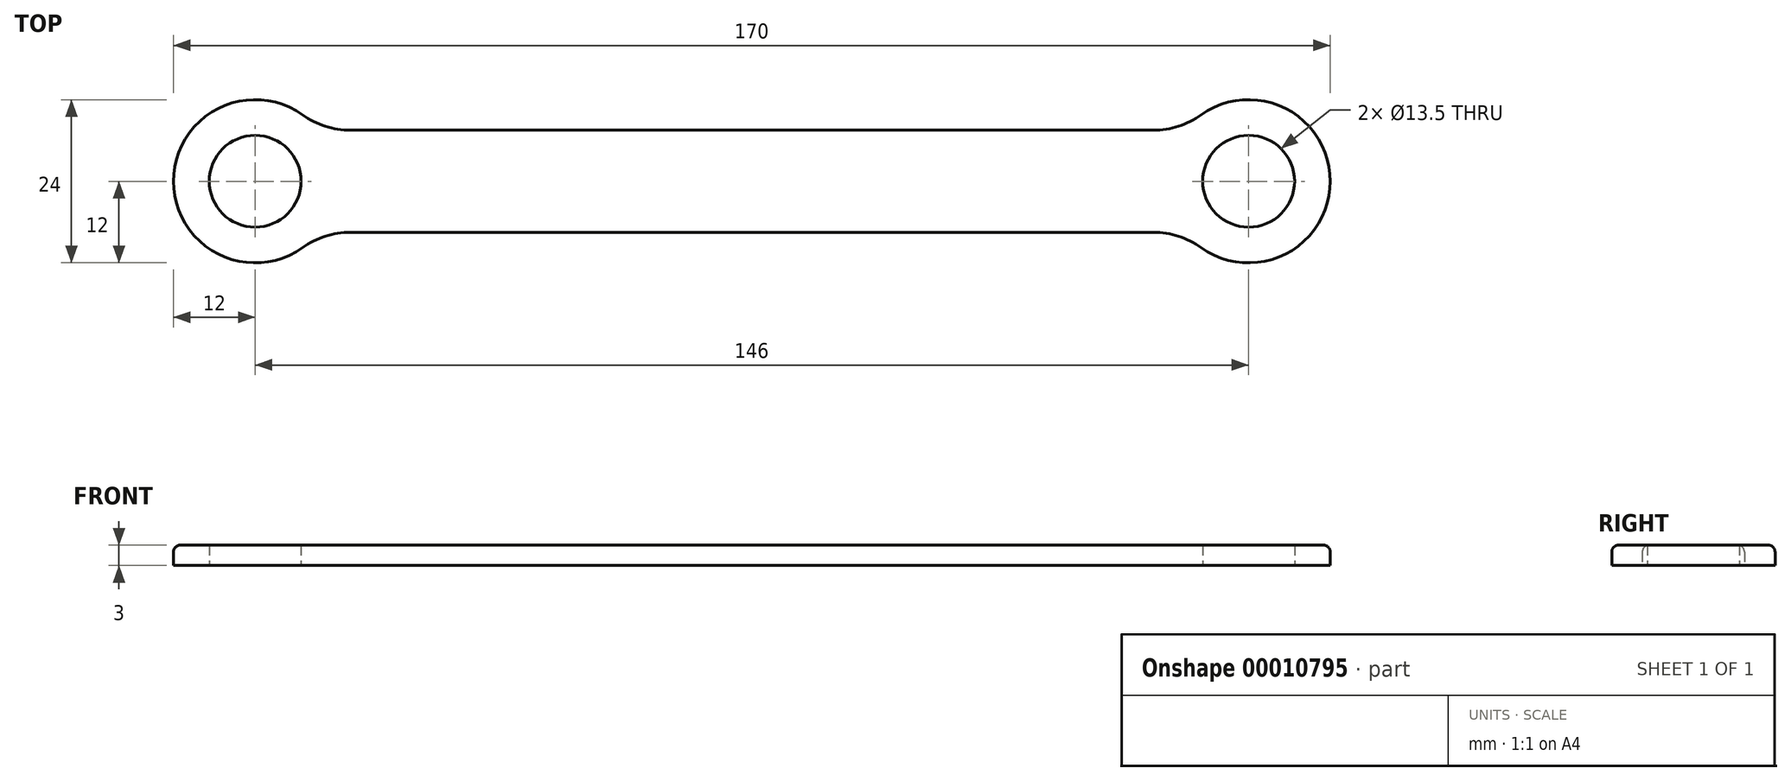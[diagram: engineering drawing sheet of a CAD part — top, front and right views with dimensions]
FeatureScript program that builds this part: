
annotation { "Feature Type Name" : "Feature", "Feature Type Description" : "" }
export const myFeature = defineFeature(function(context is Context, id is Id, definition is map)
    precondition{}
    {
        {
            var Q0;
            Q0=qCreatedBy(makeId("Top.planeOp"),FACE);
            var sketch = newSketch(context, id + "F0", { "sketchPlane" : qUnion([Q0])});
            skCircle(sketch, "E0", {"center": v(-73, 0) * mm, "radius": 6.75 * mm});
            skArc(sketch, "E1", {"start": v(-66, 9.75) * mm, "mid": v(-85, 0) * mm, "end": v(-66, -9.75) * mm});
            skLineSegment(sketch, "E2", {"start": v(0, 7.5) * mm, "end": v(-59, 7.5) * mm});
            skLineSegment(sketch, "E3", {"start": v(-59, -7.5) * mm, "end": v(0, -7.5) * mm});
            skLineSegment(sketch, "E4", {"start": v(-73, 0) * mm, "end": v(0, 0) * mm, "construction": true});
            skLineSegment(sketch, "E5", {"start": v(0, 0) * mm, "end": v(0, 32.48) * mm, "construction": true});
            skPoint(sketch, "E6.visualSharp", {"position": v(-63.63, 7.5) * mm});
            skArc(sketch, "E6.filletArc", {"start": v(-66, 9.75) * mm, "mid": v(-62.68, 8.08) * mm, "end": v(-59, 7.5) * mm});
            skPoint(sketch, "E7.visualSharp", {"position": v(-63.63, -7.5) * mm});
            skArc(sketch, "E7.filletArc", {"start": v(-59, -7.5) * mm, "mid": v(-62.68, -8.08) * mm, "end": v(-66, -9.75) * mm});
            skLineSegment(sketch, "E8.0.MirrorCS", {"start": v(0, 7.5) * mm, "end": v(59, 7.5) * mm});
            skLineSegment(sketch, "E9.0.MirrorCS", {"start": v(59, -7.5) * mm, "end": v(0, -7.5) * mm});
            skArc(sketch, "E10.0.MirrorCS", {"start": v(59, -7.5) * mm, "mid": v(62.68, -8.08) * mm, "end": v(66, -9.75) * mm});
            skArc(sketch, "E11.0.MirrorCS", {"start": v(66, 9.75) * mm, "mid": v(62.68, 8.08) * mm, "end": v(59, 7.5) * mm});
            skArc(sketch, "E12.0.MirrorCS", {"start": v(66, 9.75) * mm, "mid": v(85, 0) * mm, "end": v(66, -9.75) * mm});
            skCircle(sketch, "E13.0.MirrorC", {"center": v(73, 0) * mm, "radius": 6.75 * mm});
            skLineSegment(sketch, "E14", {"start": v(-89.97, 0) * mm, "end": v(0, 89.97) * mm, "construction": true});
            skLineSegment(sketch, "E15", {"start": v(0, 89.97) * mm, "end": v(89.97, 0) * mm, "construction": true});
            skLineSegment(sketch, "E16", {"start": v(89.97, 0) * mm, "end": v(0, -89.97) * mm, "construction": true});
            skLineSegment(sketch, "E17", {"start": v(0, -89.97) * mm, "end": v(-89.97, 0) * mm, "construction": true});
            skSolve(sketch);
        }
        {
            var Q0;
            Q0 = qSketchRegion(id + "F0", true);
            extrude(context, id + "F1", {"entities" : qUnion([Q0]), "depth" : 3 * mm});
        }
        {
            var Q0;
            Q0=makeQuery(id+"F1.opExtrude","CAP_EDGE",EDGE,{"disambiguationData":[OSD([sQuery(id+"F0.wireOp",EDGE,"E3"),sQuery(id+"F0.wireOp",EDGE,"E9.0.MirrorCS")])],"isStart":false});
            fillet(context, id + "F2", {"entities" : qUnion([Q0]), "radius" : 1 * mm, "tangentPropagation" : true, "allowEdgeOverflow" : false});
        }
    });
